# Revit family: Legrand_Transformateur_IP21_triphasé_400V-230V
name_source: partatom
category: Installations électriques
revit_build: Autodesk Revit 2018 (Build: 20170223_1515(x64)
units: mm (PartAtom-declared; Revit-internal decimal feet)

## family parameters
Basée sur le plan de construction = Non
Conserver l'orientation des annotations = Non
Cote de connecteur circulaire = Utiliser le diamètre
Couper avec des vides une fois chargée = Non
Numéro OmniClass = 23.80.00.00
Partagée = Non
Point de calcul de pièce = Non
Titre OmniClass = Electric Power and Lighting
Toujours verticalement = Oui
Type d'élément = Normal

## types (9) — shared parameters
Conditions Générale d'Utilisation = https://export.legrand.com
Fabricant = Legrand
Modèle = Transformateurs d'isolement triphasés
Tension primaire = 400 V en Δ
Tension secondaire = 230 V en Y +N
URL = www.legrand.com

## per-type parameters (varying)
| type | 042545 | 042546 | 042547 | 142536,142537, 142538, 142539 | 142548, 142549 | Poids | Section câble primaire | Section câble secondaire | Ucc (%) | diamètre de fixation | dimension A | dimension B | dimension C | fixation F | fixation G | perte totale max | perte à vide | puissance |
| Transformateur triphasé 042545 | Oui | Non | Non | Non | Non | 58.00 kg | 10 mm² | 10 mm² | 4.1 | 9 mm  [stored 0.0295276 ft] | 420 mm  [stored 1.37795 ft] | 390 mm  [stored 1.27953 ft] | 310 mm  [stored 1.01706 ft] | 400 mm  [stored 1.31234 ft] | 126 mm  [stored 0.413386 ft] | 373 W | 108 W | 6 kVA |
| Transformateur triphasé 042546 | Non | Oui | Non | Non | Non | 81.20 kg | 10 mm² | 10 mm² | 4.0 | 9 mm  [stored 0.0295276 ft] | 470 mm  [stored 1.54199 ft] | 410 mm  [stored 1.34514 ft] | 310 mm  [stored 1.01706 ft] | 450 mm  [stored 1.47638 ft] | 146 mm  [stored 0.479003 ft] | 596 W | 188 W | 10 kVA |
| Transformateur triphasé 042547 | Non | Non | Oui | Non | Non | 110.50 kg | 35 mm² | 35 mm² | 4.4 | 9 mm  [stored 0.0295276 ft] | 530 mm  [stored 1.73885 ft] | 460 mm  [stored 1.50919 ft] | 380 mm  [stored 1.24672 ft] | 510 mm  [stored 1.67323 ft] | 136 mm | 922 W | 236 W | 16 kVA |
| Transformateur triphasé 142548 | Non | Non | Non | Non | Oui | 127.00 kg | 35 mm² | 35 mm² | 3.6 | 11 mm  [stored 0.0360892 ft] | 590 mm  [stored 1.9357 ft] | 650 mm  [stored 2.13255 ft] | 500 mm  [stored 1.64042 ft] | 570 mm  [stored 1.87008 ft] | 146 mm  [stored 0.479003 ft] | 1018 W | 210 W | 25 kVA |
| Transformateur triphasé 142549 | Non | Non | Non | Non | Oui | 172.00 kg | 35 mm² | 70 mm² | 3.6 | 11 mm  [stored 0.0360892 ft] | 590 mm  [stored 1.9357 ft] | 650 mm  [stored 2.13255 ft] | 500 mm  [stored 1.64042 ft] | 570 mm  [stored 1.87008 ft] | 176 mm  [stored 0.577428 ft] | 1521 W | 330 W | 40 kVA |
| Transformateur triphasé 142536 | Non | Non | Non | Oui | Non | 247.00 kg | 35 mm² | 70 mm² | 5.5 | 16 mm  [stored 0.0524934 ft] | 670 mm  [stored 2.19816 ft] | 700 mm  [stored 2.29659 ft] | 610 mm  [stored 2.00131 ft] | 400 mm  [stored 1.31234 ft] | 580 mm  [stored 1.90289 ft] | 2768 W | 427 W | 50 kVA |
| Transformateur triphasé 142537 | Non | Non | Non | Oui | Non | 271.00 kg | 35 mm² | 120 mm² | 5.4 | 16 mm  [stored 0.0524934 ft] | 670 mm  [stored 2.19816 ft] | 700 mm  [stored 2.29659 ft] | 610 mm  [stored 2.00131 ft] | 400 mm  [stored 1.31234 ft] | 580 mm  [stored 1.90289 ft] | 2798 W | 486 W | 63 kVA |
| Transformateur triphasé 142538 | Non | Non | Non | Oui | Non | 330.00 kg | 70 mm² | 120 mm² | 5.0 | 16 mm  [stored 0.0524934 ft] | 670 mm  [stored 2.19816 ft] | 800 mm  [stored 2.62467 ft] | 740 mm  [stored 2.42782 ft] | 400 mm  [stored 1.31234 ft] | 687 mm  [stored 2.25394 ft] | 2767 W | 578 W | 80 kVA |
| Transformateur triphasé 142539 | Non | Non | Non | Oui | Non | 401.00 kg | 120 mm² | 120 mm² | 3.9 | 16 mm  [stored 0.0524934 ft] | 670 mm  [stored 2.19816 ft] | 800 mm  [stored 2.62467 ft] | 740 mm  [stored 2.42782 ft] | 400 mm  [stored 1.31234 ft] | 687 mm  [stored 2.25394 ft] | 3260 W | 733 W | 100 kVA |

note: [stored X ft] marks values corroborated as IEEE doubles in the binary element streams (Revit-internal decimal feet)
